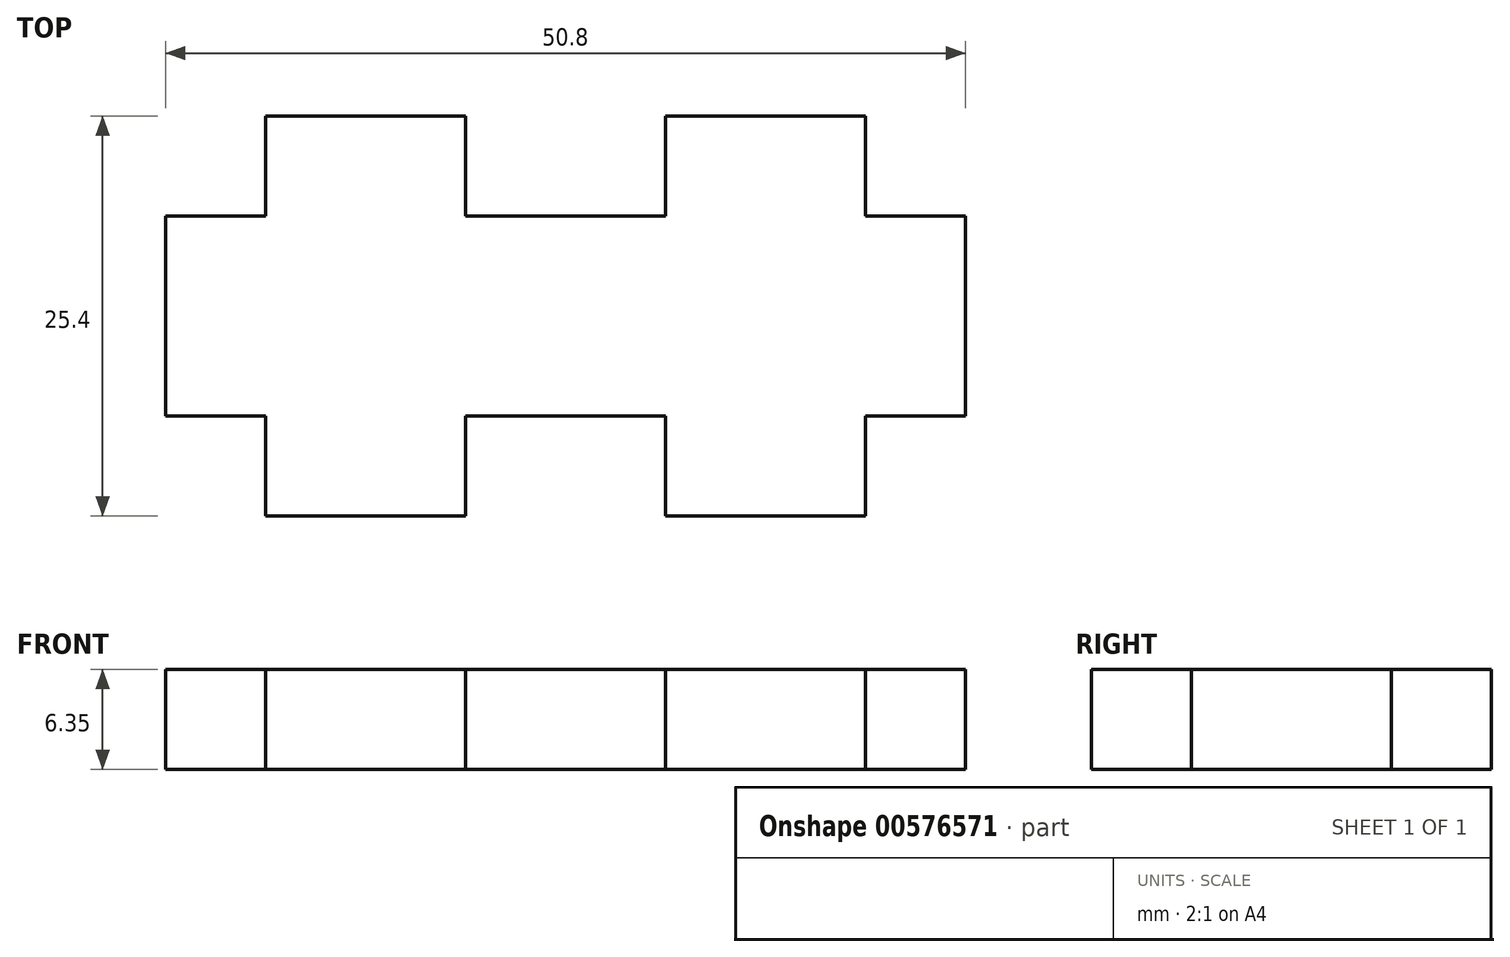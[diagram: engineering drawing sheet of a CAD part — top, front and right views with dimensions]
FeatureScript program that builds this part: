
annotation { "Feature Type Name" : "Feature", "Feature Type Description" : "" }
export const myFeature = defineFeature(function(context is Context, id is Id, definition is map)
    precondition{}
    {
        {
            var Q0;
            Q0=qCreatedBy(makeId("Top.planeOp"),FACE);
            var sketch = newSketch(context, id + "F0", { "sketchPlane" : qUnion([Q0])});
            skLineSegment(sketch, "E0.top", {"start": v(12.7, -25.4) * mm, "end": v(25.4, -25.4) * mm});
            skLineSegment(sketch, "E1", {"start": v(12.7, -6.35) * mm, "end": v(12.7, 0) * mm});
            skLineSegment(sketch, "E2", {"start": v(12.7, 0) * mm, "end": v(25.4, 0) * mm});
            skLineSegment(sketch, "E3", {"start": v(25.4, 0) * mm, "end": v(25.4, -6.35) * mm});
            skLineSegment(sketch, "E4", {"start": v(25.4, -6.35) * mm, "end": v(38.1, -6.35) * mm});
            skLineSegment(sketch, "E5", {"start": v(38.1, -6.35) * mm, "end": v(38.1, 0) * mm});
            skLineSegment(sketch, "E6", {"start": v(38.1, 0) * mm, "end": v(50.8, 0) * mm});
            skLineSegment(sketch, "E7", {"start": v(50.8, 0) * mm, "end": v(50.8, -6.35) * mm});
            skPoint(sketch, "E8.orphan", {"position": v(0, 0) * mm});
            skPoint(sketch, "E9.orphan", {"position": v(63.5, 0) * mm});
            skLineSegment(sketch, "E10", {"start": v(12.7, -19.05) * mm, "end": v(12.7, -25.4) * mm});
            skPoint(sketch, "E11.orphan", {"position": v(0, -25.4) * mm});
            skPoint(sketch, "E12.orphan", {"position": v(6.35, -6.35) * mm});
            skLineSegment(sketch, "E13", {"start": v(25.4, -25.4) * mm, "end": v(25.4, -19.05) * mm});
            skLineSegment(sketch, "E14", {"start": v(25.4, -19.05) * mm, "end": v(38.1, -19.05) * mm});
            skLineSegment(sketch, "E15", {"start": v(38.1, -19.05) * mm, "end": v(38.1, -25.4) * mm});
            skLineSegment(sketch, "E16", {"start": v(38.1, -25.4) * mm, "end": v(50.8, -25.4) * mm});
            skLineSegment(sketch, "E17", {"start": v(50.8, -25.4) * mm, "end": v(50.8, -19.05) * mm});
            skLineSegment(sketch, "E18", {"start": v(12.7, -6.35) * mm, "end": v(6.35, -6.35) * mm});
            skLineSegment(sketch, "E19", {"start": v(6.35, -6.35) * mm, "end": v(6.35, -19.05) * mm});
            skLineSegment(sketch, "E20", {"start": v(6.35, -19.05) * mm, "end": v(12.7, -19.05) * mm});
            skLineSegment(sketch, "E21", {"start": v(50.8, -6.35) * mm, "end": v(57.15, -6.35) * mm});
            skLineSegment(sketch, "E22", {"start": v(57.15, -6.35) * mm, "end": v(57.15, -19.05) * mm});
            skLineSegment(sketch, "E23", {"start": v(57.15, -19.05) * mm, "end": v(50.8, -19.05) * mm});
            skSolve(sketch);
        }
        {
            var Q0;
            Q0=makeQuery(id+"F0.imprint","IMPRINT",FACE,{"disambiguationData":[TD([[makeQuery(id+"F0.imprint","IMPRINT",EDGE,{"derivedFrom":sQuery(id+"F0.wireOp",EDGE,"E1")}),-1.0]])]});
            extrude(context, id + "F1", {"entities" : qUnion([Q0]), "depth" : 6.35 * mm, "offsetDistance" : 25.4 * mm});
        }
    });
